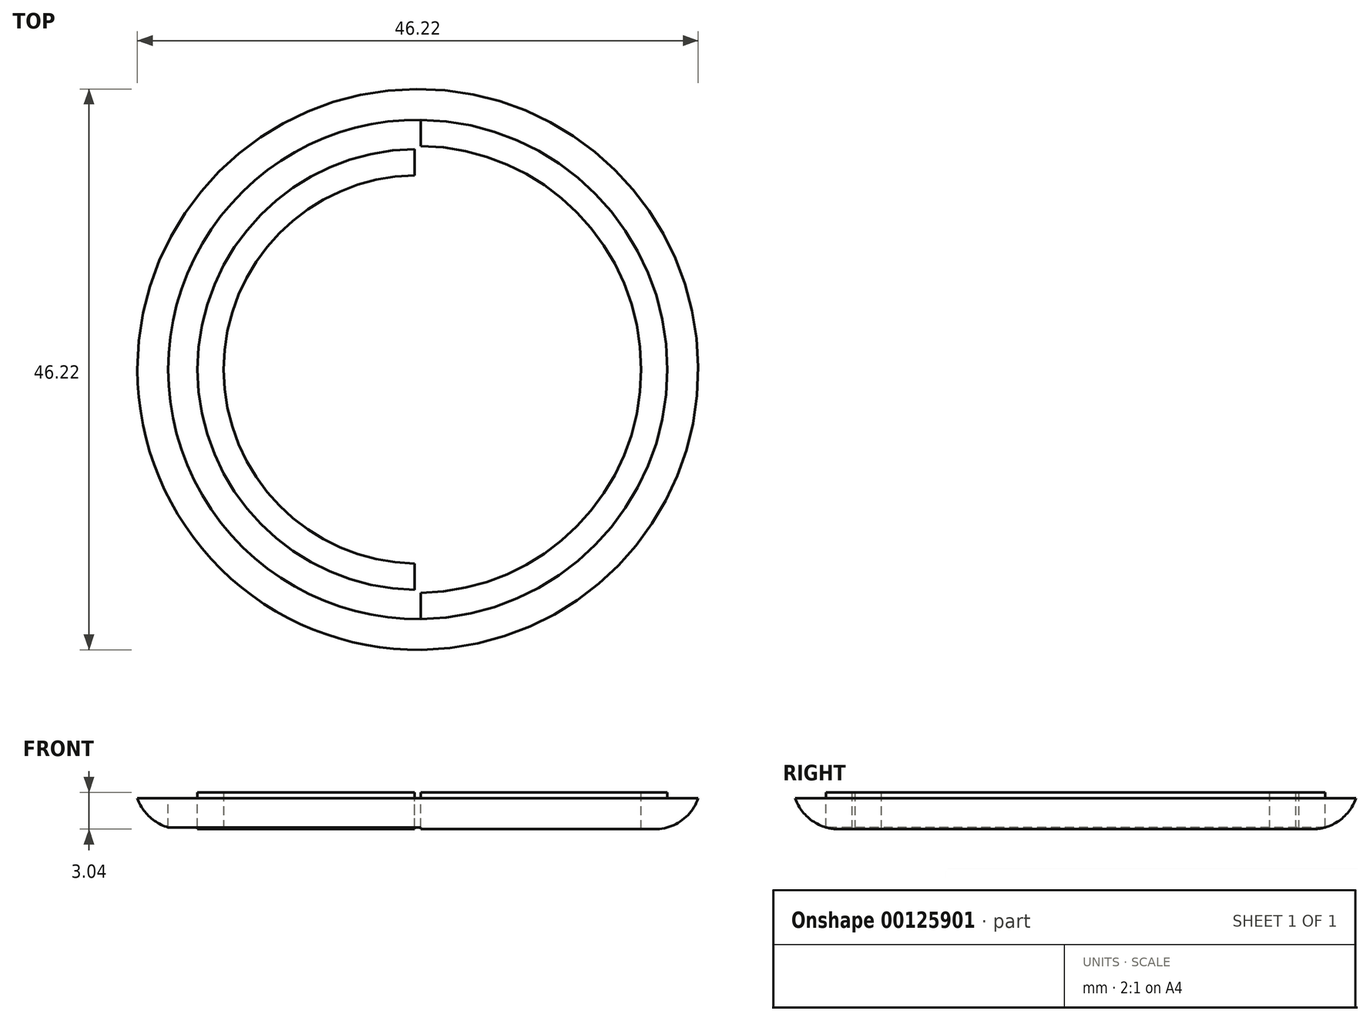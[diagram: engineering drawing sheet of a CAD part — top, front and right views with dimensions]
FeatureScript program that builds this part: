
annotation { "Feature Type Name" : "Feature", "Feature Type Description" : "" }
export const myFeature = defineFeature(function(context is Context, id is Id, definition is map)
    precondition{}
    {
        {
            var Q0;
            Q0=qCreatedBy(makeId("Top.planeOp"),FACE);
            var sketch = newSketch(context, id + "F0", { "sketchPlane" : qUnion([Q0])});
            skCircle(sketch, "E0", {"center": v(0, 0) * mm, "radius": 16 * mm});
            skCircle(sketch, "E1.0", {"center": v(0, 0) * mm, "radius": 20.57 * mm});
            skSolve(sketch);
        }
        {
            var Q0;
            Q0=makeQuery(id+"F0.imprint","IMPRINT",FACE,{"disambiguationData":[TD([[makeQuery(id+"F0.imprint","IMPRINT",EDGE,{"derivedFrom":sQuery(id+"F0.wireOp",EDGE,"E0")}),-1.0]])]});
            extrude(context, id + "F1", {"entities" : qUnion([Q0]), "depth" : ((.75 / 3) * 2) * mm});
        }
        {
            var Q0;
            Q0=makeQuery(id+"F1.opExtrude","CAP_FACE",FACE,{"disambiguationData":[OSD([sQuery(id+"F0.wireOp",EDGE,"E0"),sQuery(id+"F0.wireOp",EDGE,"E1.0")])],"isStart":true});
            var sketch = newSketch(context, id + "F2", { "sketchPlane" : qUnion([Q0])});
            skCircle(sketch, "E2.0", {"center": v(0, 0) * mm, "radius": 23.11 * mm});
            skSolve(sketch);
        }
        {
            var Q0;
            Q0=makeQuery(id+"F2.imprint","IMPRINT",FACE,{"disambiguationData":[TD([[makeQuery(id+"F2.imprint","IMPRINT",EDGE,{"derivedFrom":sQuery(id+"F2.wireOp",EDGE,"E2.0")}),1.0]])]});
            var Q1;
            Q1=makeQuery(id+"F2.imprint","IMPRINT",FACE,{"disambiguationData":[TD([[makeQuery(id+"F2.imprint","IMPRINT",EDGE,{"derivedFrom":makeQuery(id+"F1.opExtrude","CAP_EDGE",EDGE,{"disambiguationData":[OSD([sQuery(id+"F0.wireOp",EDGE,"E0")])],"isStart":true})}),1.0]])]});
            extrude(context, id + "F3", {"entities" : qUnion([Q0, Q1]), "operationType" : NewBodyOperationType.ADD, "depth" : 2.54 * mm});
        }
        {
            var Q0;
            Q0=makeQuery(id+"F3.opExtrude","CAP_EDGE",EDGE,{"disambiguationData":[OSD([sQuery(id+"F2.wireOp",EDGE,"E2.0")])],"isStart":false});
            fillet(context, id + "F4", {"entities" : qUnion([Q0]), "radius" : 3.8 * mm, "tangentPropagation" : true, "allowEdgeOverflow" : false});
        }
        {
            var Q0;
            Q0=makeQuery(id+"F1.opExtrude","CAP_FACE",FACE,{"disambiguationData":[OSD([sQuery(id+"F0.wireOp",EDGE,"E0"),sQuery(id+"F0.wireOp",EDGE,"E1.0")])],"isStart":false});
            var sketch = newSketch(context, id + "F5", { "sketchPlane" : qUnion([Q0])});
            skCircle(sketch, "E3.0", {"center": v(0, 0) * mm, "radius": 18.41 * mm});
            skCircle(sketch, "E4.0", {"center": v(0, 0) * mm, "radius": 18.16 * mm});
            skLineSegment(sketch, "E5", {"start": v(0, 21.42) * mm, "end": v(0, -21.7) * mm, "construction": true});
            skLineSegment(sketch, "E6", {"start": v(0, 0) * mm, "end": v(-0.25, 0) * mm, "construction": true});
            skLineSegment(sketch, "E7", {"start": v(18.41, 0) * mm, "end": v(18.16, 0) * mm, "construction": true});
            skLineSegment(sketch, "E8", {"start": v(-0.25, 0) * mm, "end": v(-0.25, 21.42) * mm, "construction": true});
            skLineSegment(sketch, "E9", {"start": v(-0.25, 20.57) * mm, "end": v(-0.25, 18.41) * mm});
            skLineSegment(sketch, "E10", {"start": v(-0.25, 18.41) * mm, "end": v(-0.25, 18.16) * mm});
            skLineSegment(sketch, "E11", {"start": v(-0.25, 18.16) * mm, "end": v(-0.25, 16) * mm});
            skLineSegment(sketch, "E12.MirrorCS", {"start": v(0.25, 0) * mm, "end": v(0.25, 21.42) * mm, "construction": true});
            skLineSegment(sketch, "E13", {"start": v(0.25, 20.57) * mm, "end": v(0.25, 18.41) * mm});
            skLineSegment(sketch, "E14", {"start": v(0.25, 18.41) * mm, "end": v(0.25, 18.16) * mm});
            skLineSegment(sketch, "E15", {"start": v(0.25, 18.16) * mm, "end": v(0.25, 16) * mm});
            skLineSegment(sketch, "E16", {"start": v(-21.53, 0) * mm, "end": v(21.8, 0) * mm, "construction": true});
            skLineSegment(sketch, "E17.MirrorCS", {"start": v(0.25, 0) * mm, "end": v(0.25, -21.42) * mm, "construction": true});
            skLineSegment(sketch, "E18.MirrorCS", {"start": v(-0.25, 0) * mm, "end": v(-0.25, -21.42) * mm, "construction": true});
            skLineSegment(sketch, "E19", {"start": v(0.25, -20.57) * mm, "end": v(0.25, -18.41) * mm});
            skLineSegment(sketch, "E20", {"start": v(0.25, -18.41) * mm, "end": v(0.25, -18.16) * mm});
            skLineSegment(sketch, "E21", {"start": v(0.25, -18.16) * mm, "end": v(0.25, -16) * mm});
            skLineSegment(sketch, "E22", {"start": v(-0.25, -16) * mm, "end": v(-0.25, -18.16) * mm});
            skLineSegment(sketch, "E23", {"start": v(-0.25, -18.16) * mm, "end": v(-0.25, -18.41) * mm});
            skLineSegment(sketch, "E24", {"start": v(-0.25, -18.41) * mm, "end": v(-0.25, -20.57) * mm});
            skSolve(sketch);
        }
        {
            var Q0;
            {var subQ0=sQuery(id+"F5.wireOp",EDGE,"E9");Q0=makeQuery(id+"F5.imprint","IMPRINT",FACE,{"disambiguationData":[TD([[makeQuery(id+"F5.imprint","IMPRINT",EDGE,{"derivedFrom":subQ0}),-1.0]])]});}
            var Q1;
            {var subQ0=sQuery(id+"F5.wireOp",EDGE,"E15");Q1=makeQuery(id+"F5.imprint","IMPRINT",FACE,{"disambiguationData":[TD([[makeQuery(id+"F5.imprint","IMPRINT",EDGE,{"derivedFrom":subQ0}),1.0]])]});}
            var Q2;
            {var subQ0=sQuery(id+"F5.wireOp",EDGE,"E11");Q2=makeQuery(id+"F5.imprint","IMPRINT",FACE,{"disambiguationData":[TD([[makeQuery(id+"F5.imprint","IMPRINT",EDGE,{"derivedFrom":subQ0}),1.0]])]});}
            var Q3;
            {var subQ0=sQuery(id+"F5.wireOp",EDGE,"E10");Q3=makeQuery(id+"F5.imprint","IMPRINT",FACE,{"disambiguationData":[TD([[makeQuery(id+"F5.imprint","IMPRINT",EDGE,{"derivedFrom":subQ0}),1.0]])]});}
            var Q4;
            {var subQ0=sQuery(id+"F5.wireOp",EDGE,"E9");Q4=makeQuery(id+"F5.imprint","IMPRINT",FACE,{"disambiguationData":[TD([[makeQuery(id+"F5.imprint","IMPRINT",EDGE,{"derivedFrom":subQ0}),1.0]])]});}
            var Q5;
            {var subQ0=sQuery(id+"F5.wireOp",EDGE,"E21");Q5=makeQuery(id+"F5.imprint","IMPRINT",FACE,{"disambiguationData":[TD([[makeQuery(id+"F5.imprint","IMPRINT",EDGE,{"derivedFrom":subQ0}),1.0]])]});}
            var Q6;
            {var subQ0=sQuery(id+"F5.wireOp",EDGE,"E20");Q6=makeQuery(id+"F5.imprint","IMPRINT",FACE,{"disambiguationData":[TD([[makeQuery(id+"F5.imprint","IMPRINT",EDGE,{"derivedFrom":subQ0}),1.0]])]});}
            var Q7;
            {var subQ0=sQuery(id+"F5.wireOp",EDGE,"E19");Q7=makeQuery(id+"F5.imprint","IMPRINT",FACE,{"disambiguationData":[TD([[makeQuery(id+"F5.imprint","IMPRINT",EDGE,{"derivedFrom":subQ0}),1.0]])]});}
            var Q8;
            {var subQ0=sQuery(id+"F5.wireOp",EDGE,"E10");Q8=makeQuery(id+"F5.imprint","IMPRINT",FACE,{"disambiguationData":[TD([[makeQuery(id+"F5.imprint","IMPRINT",EDGE,{"derivedFrom":subQ0}),-1.0]])]});}
            var Q9;
            {var subQ0=sQuery(id+"F5.wireOp",EDGE,"E14");Q9=makeQuery(id+"F5.imprint","IMPRINT",FACE,{"disambiguationData":[TD([[makeQuery(id+"F5.imprint","IMPRINT",EDGE,{"derivedFrom":subQ0}),1.0]])]});}
            extrude(context, id + "F6", {"entities" : qUnion([Q0, Q1, Q2, Q3, Q4, Q5, Q6, Q7, Q8, Q9]), "operationType" : NewBodyOperationType.REMOVE, "oppositeDirection" : true, "depth" : 6.35 * mm});
        }
    });
